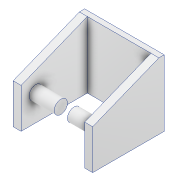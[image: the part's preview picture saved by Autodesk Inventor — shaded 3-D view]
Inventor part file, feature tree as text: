
AUTODESK INVENTOR PART (.ipt)
format: ipt  version: 2020 (Build 240168000, 168)  size: 185,856 bytes
history: native  units: mm
features: extrude x8, sketch x8, projected_geometry x4, other x1
ambient origin geometry x8: Origin, YZ Plane, XZ Plane, XY Plane, X Axis, Y Axis, Z Axis, Center Point
bodies: Body1 (feature_tree)
feature tree (21):
  other  "솔리드1"
  extrude  "돌출1"  Depth=30.0mm
  extrude  "돌출2"  Depth=30.0mm
  extrude  "돌출3"  Depth=2.0mm TaperAngle=0.0deg
  extrude  "돌출4"  Depth=3.0mm
  extrude  "돌출5"  Depth=3.0mm
  extrude  "돌출6"  Depth=30.0mm TaperAngle=0.0deg
  extrude  "돌출7"  Depth=10.0mm
  extrude  "돌출8"  Depth=1.0mm TaperAngle=0.0deg
  sketch  "스케치1"
  sketch  "스케치2"
  sketch  "스케치3"
  sketch  "스케치4"
  sketch  "스케치5"
  sketch  "스케치6"
  projected_geometry  "투영된 루프1"
  projected_geometry  "투영된 루프2"
  sketch  "스케치7"
  projected_geometry  "투영된 루프3"
  sketch  "스케치8"
  projected_geometry  "투영된 루프4"
